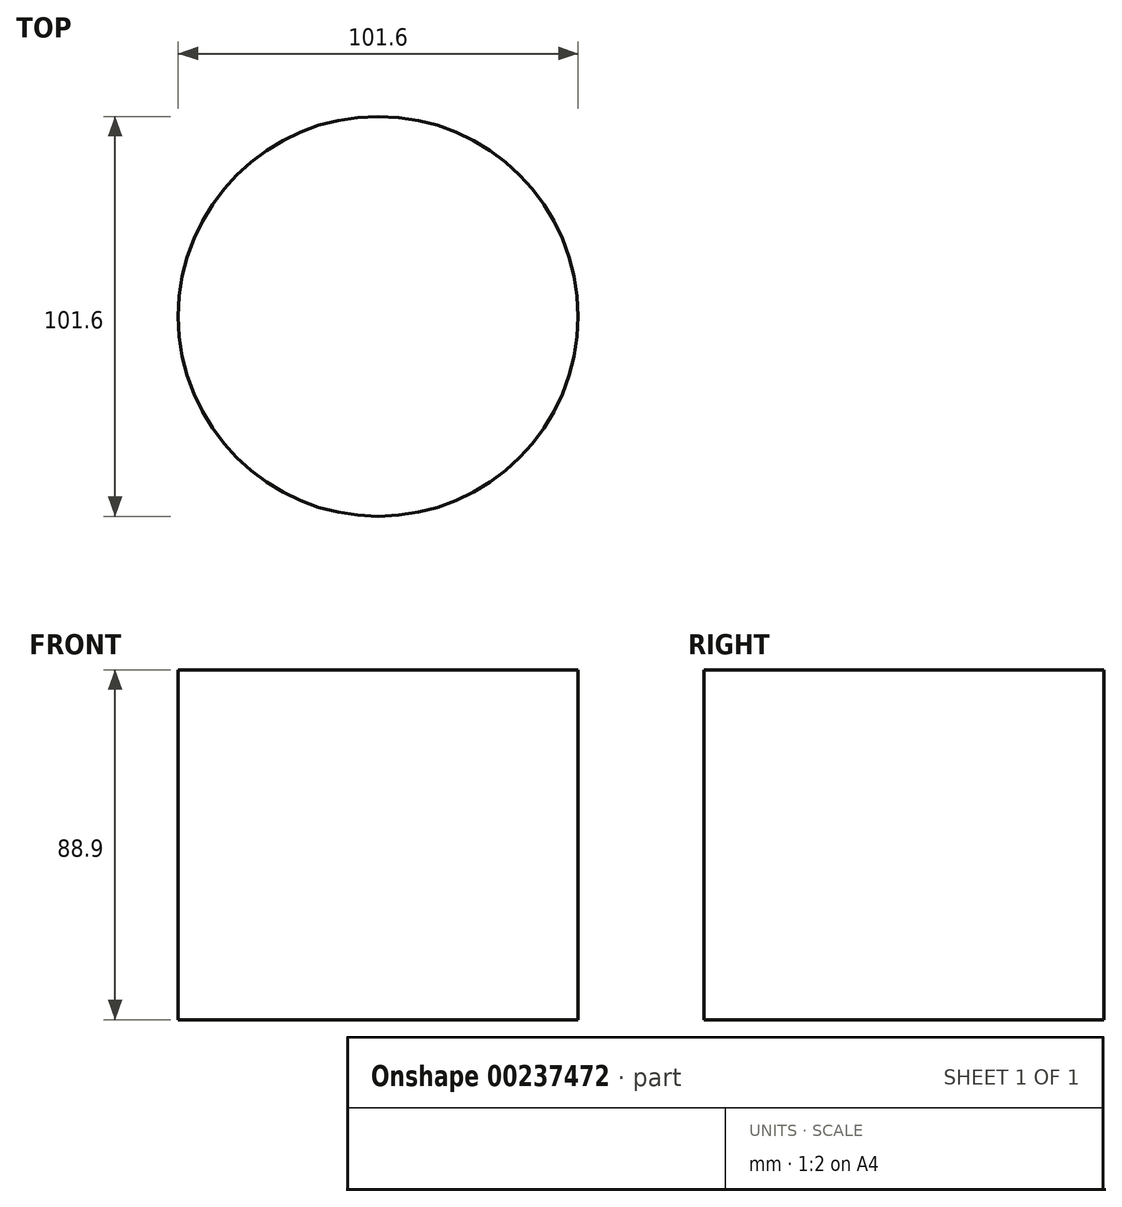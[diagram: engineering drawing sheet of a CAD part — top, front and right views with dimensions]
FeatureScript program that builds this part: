
annotation { "Feature Type Name" : "Feature", "Feature Type Description" : "" }
export const myFeature = defineFeature(function(context is Context, id is Id, definition is map)
    precondition{}
    {
        {
            var Q0;
            Q0=qCreatedBy(makeId("Top.planeOp"),FACE);
            var sketch = newSketch(context, id + "F0", { "sketchPlane" : qUnion([Q0])});
            skCircle(sketch, "E0", {"center": v(0, 0) * mm, "radius": 50.8 * mm});
            skSolve(sketch);
        }
        {
            var Q0;
            Q0 = qSketchRegion(id + "F0", true);
            extrude(context, id + "F1", {"entities" : qUnion([Q0]), "depth" : 88.9 * mm});
        }
    });
